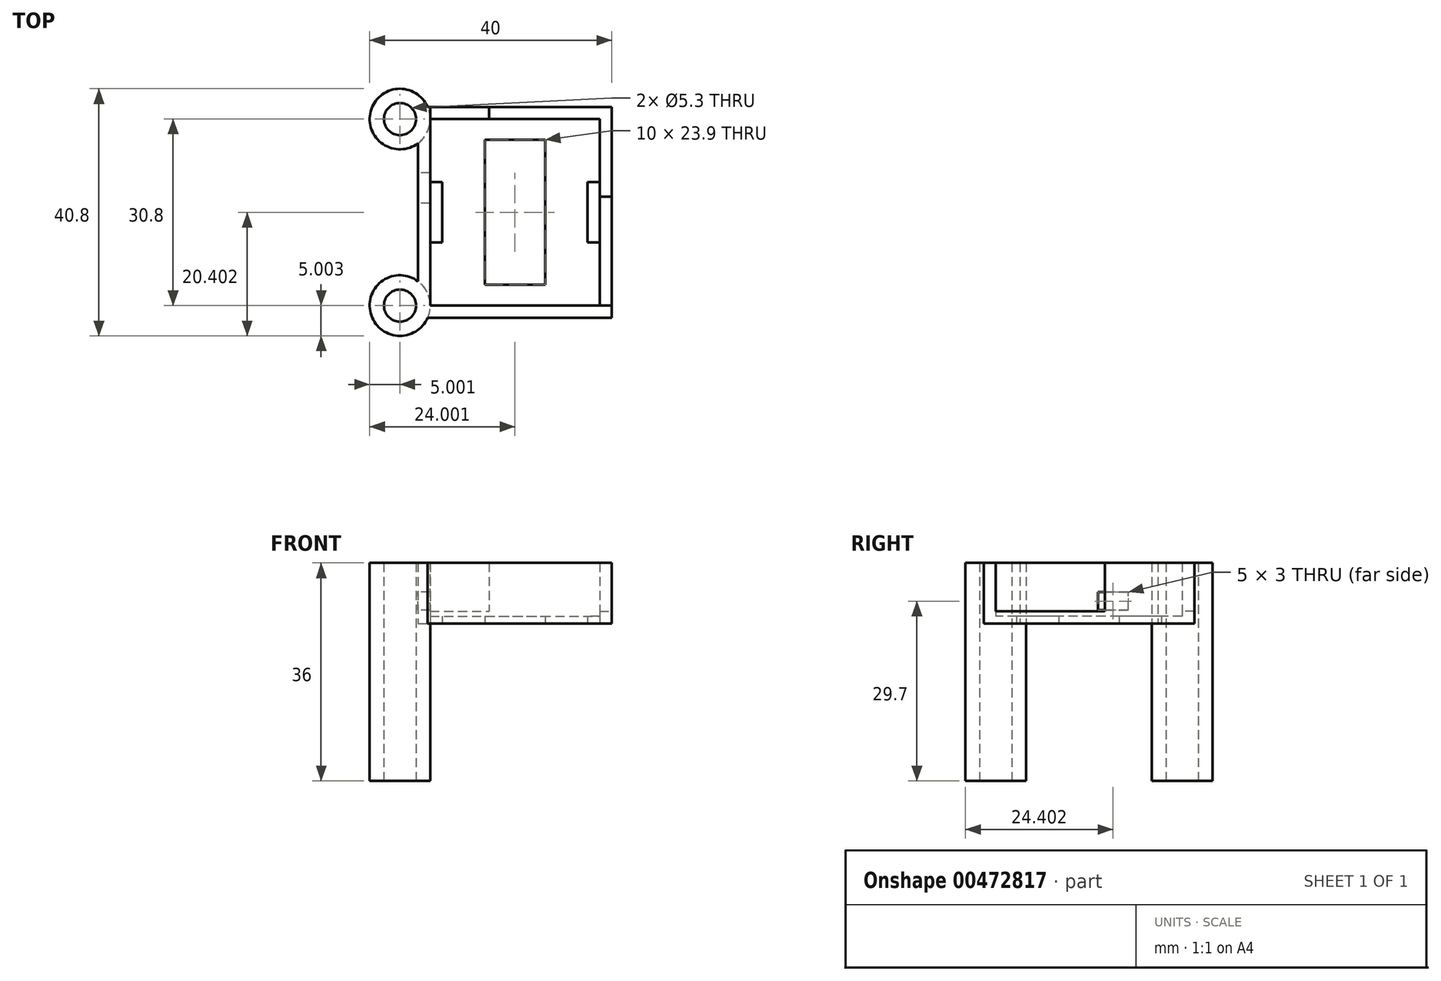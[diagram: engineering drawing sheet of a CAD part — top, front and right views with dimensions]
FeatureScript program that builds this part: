
annotation { "Feature Type Name" : "Feature", "Feature Type Description" : "" }
export const myFeature = defineFeature(function(context is Context, id is Id, definition is map)
    precondition{}
    {
        {
            var Q0;
            Q0=qCreatedBy(makeId("Top.planeOp"),FACE);
            var sketch = newSketch(context, id + "F0", { "sketchPlane" : qUnion([Q0])});
            skCircle(sketch, "E0", {"center": v(-36.74, -17.75) * mm, "radius": 5 * mm});
            skCircle(sketch, "E1", {"center": v(-36.74, 13.05) * mm, "radius": 5 * mm});
            skCircle(sketch, "E2", {"center": v(-36.74, -17.75) * mm, "radius": 2.65 * mm});
            skCircle(sketch, "E3", {"center": v(-36.74, 13.05) * mm, "radius": 2.65 * mm});
            skLineSegment(sketch, "E4", {"start": v(-36.74, 13.05) * mm, "end": v(-36.74, -17.75) * mm, "construction": true});
            skLineSegment(sketch, "E5.bottom", {"start": v(-31.74, 13.05) * mm, "end": v(-3.74, 13.05) * mm});
            skLineSegment(sketch, "E5.top", {"start": v(-31.74, -17.75) * mm, "end": v(-3.74, -17.75) * mm});
            skLineSegment(sketch, "E5.left", {"start": v(-31.74, 13.05) * mm, "end": v(-31.74, -17.75) * mm});
            skLineSegment(sketch, "E5.right", {"start": v(-3.74, 13.05) * mm, "end": v(-3.74, -17.75) * mm});
            skLineSegment(sketch, "E6", {"start": v(-36.74, -2.35) * mm, "end": v(-1.24, -2.35) * mm, "construction": true});
            skLineSegment(sketch, "E7", {"start": v(-17.74, 13.05) * mm, "end": v(-17.74, -17.75) * mm, "construction": true});
            skLineSegment(sketch, "E8.bottom", {"start": v(-33.74, 15.05) * mm, "end": v(-1.74, 15.05) * mm});
            skLineSegment(sketch, "E8.top", {"start": v(-33.74, -19.75) * mm, "end": v(-1.74, -19.75) * mm});
            skLineSegment(sketch, "E8.left", {"start": v(-33.74, 15.05) * mm, "end": v(-33.74, -19.75) * mm});
            skLineSegment(sketch, "E8.right", {"start": v(-1.74, 15.05) * mm, "end": v(-1.74, -19.75) * mm});
            skLineSegment(sketch, "E9.bottom", {"start": v(-22.74, 9.6) * mm, "end": v(-12.74, 9.6) * mm});
            skLineSegment(sketch, "E9.top", {"start": v(-22.74, -14.3) * mm, "end": v(-12.74, -14.3) * mm});
            skLineSegment(sketch, "E9.left", {"start": v(-22.74, 9.6) * mm, "end": v(-22.74, -14.3) * mm});
            skLineSegment(sketch, "E9.right", {"start": v(-12.74, 9.6) * mm, "end": v(-12.74, -14.3) * mm});
            skLineSegment(sketch, "E10.bottom", {"start": v(-3.74, 2.65) * mm, "end": v(-5.74, 2.65) * mm});
            skLineSegment(sketch, "E10.top", {"start": v(-3.74, -7.35) * mm, "end": v(-5.74, -7.35) * mm});
            skLineSegment(sketch, "E10.left", {"start": v(-3.74, 2.65) * mm, "end": v(-3.74, -7.35) * mm});
            skLineSegment(sketch, "E10.right", {"start": v(-5.74, 2.65) * mm, "end": v(-5.74, -7.35) * mm});
            skLineSegment(sketch, "E11.bottom", {"start": v(-31.74, 2.65) * mm, "end": v(-29.74, 2.65) * mm});
            skLineSegment(sketch, "E11.top", {"start": v(-31.74, -7.35) * mm, "end": v(-29.74, -7.35) * mm});
            skLineSegment(sketch, "E11.left", {"start": v(-31.74, 2.65) * mm, "end": v(-31.74, -7.35) * mm});
            skLineSegment(sketch, "E11.right", {"start": v(-29.74, 2.65) * mm, "end": v(-29.74, -7.35) * mm});
            skSolve(sketch);
        }
        {
            var Q0;
            Q0=makeQuery(id+"F0.imprint","IMPRINT",FACE,{"disambiguationData":[TD([[makeQuery(id+"F0.imprint","IMPRINT",EDGE,{"derivedFrom":sQuery(id+"F0.wireOp",EDGE,"E5.bottom")}),-1.0]])]});
            extrude(context, id + "F1", {"entities" : qUnion([Q0]), "depth" : 1.2 * mm});
        }
        {
            var Q0;
            {var subQ1=sQuery(id+"F0.wireOp",EDGE,"E5.bottom");Q0=makeQuery(id+"F0.imprint","IMPRINT",FACE,{"disambiguationData":[TD([[makeQuery(id+"F0.imprint","IMPRINT",EDGE,{"derivedFrom":subQ1}),1.0]])]});}
            var Q1;
            {var subQ0=sQuery(id+"F0.wireOp",EDGE,"E5.left");Q1=makeQuery(id+"F0.imprint","IMPRINT",FACE,{"disambiguationData":[TD([[makeQuery(id+"F0.imprint","IMPRINT",EDGE,{"derivedFrom":subQ0}),-1.0]])]});}
            var Q2;
            {var subQ2=sQuery(id+"F0.wireOp",EDGE,"E8.left");var subQ4=sQuery(id+"F0.wireOp",EDGE,"E8.bottom");var subQ6=makeQuery(id+"F0.imprint","INTERSECT",VERTEX,{"derivedFrom":[subQ4,subQ2]});Q2=makeQuery(id+"F0.imprint","IMPRINT",FACE,{"disambiguationData":[TD([[makeQuery(id+"F0.imprint","IMPRINT",EDGE,{"disambiguationData":[TD([[subQ6,-1.0]])],"derivedFrom":subQ4}),-1.0]])]});}
            var Q3;
            {var subQ0=sQuery(id+"F0.wireOp",EDGE,"E0");var subQ2=makeQuery(id+"F0.imprint","INTERSECT",VERTEX,{"derivedFrom":[subQ0,sQuery(id+"F0.wireOp",EDGE,"E5.left")]});Q3=makeQuery(id+"F0.imprint","IMPRINT",FACE,{"disambiguationData":[TD([[makeQuery(id+"F0.imprint","IMPRINT",EDGE,{"disambiguationData":[TD([[subQ2,-1.0]])],"derivedFrom":subQ0}),1.0]])]});}
            extrude(context, id + "F2", {"entities" : qUnion([Q0, Q1, Q2, Q3]), "operationType" : NewBodyOperationType.ADD, "depth" : 10 * mm});
        }
        {
            var Q0;
            Q0=makeQuery(id+"F0.imprint","IMPRINT",FACE,{"disambiguationData":[TD([[makeQuery(id+"F0.imprint","IMPRINT",EDGE,{"derivedFrom":sQuery(id+"F0.wireOp",EDGE,"E3")}),-1.0]])]});
            var Q1;
            Q1=makeQuery(id+"F0.imprint","IMPRINT",FACE,{"disambiguationData":[TD([[makeQuery(id+"F0.imprint","IMPRINT",EDGE,{"derivedFrom":sQuery(id+"F0.wireOp",EDGE,"E2")}),-1.0]])]});
            extrude(context, id + "F3", {"entities" : qUnion([Q0, Q1]), "operationType" : NewBodyOperationType.ADD, "depth" : 10 * mm});
        }
        {
            var Q0;
            Q0=makeQuery(id+"F0.imprint","IMPRINT",FACE,{"disambiguationData":[TD([[makeQuery(id+"F0.imprint","IMPRINT",EDGE,{"derivedFrom":sQuery(id+"F0.wireOp",EDGE,"E3")}),-1.0]])]});
            var Q1;
            {var subQ2=sQuery(id+"F0.wireOp",EDGE,"E8.left");var subQ4=sQuery(id+"F0.wireOp",EDGE,"E8.bottom");var subQ6=makeQuery(id+"F0.imprint","INTERSECT",VERTEX,{"derivedFrom":[subQ4,subQ2]});Q1=makeQuery(id+"F0.imprint","IMPRINT",FACE,{"disambiguationData":[TD([[makeQuery(id+"F0.imprint","IMPRINT",EDGE,{"disambiguationData":[TD([[subQ6,-1.0]])],"derivedFrom":subQ4}),-1.0]])]});}
            var Q2;
            Q2=makeQuery(id+"F0.imprint","IMPRINT",FACE,{"disambiguationData":[TD([[makeQuery(id+"F0.imprint","IMPRINT",EDGE,{"derivedFrom":sQuery(id+"F0.wireOp",EDGE,"E2")}),-1.0]])]});
            var Q3;
            {var subQ0=sQuery(id+"F0.wireOp",EDGE,"E0");var subQ2=makeQuery(id+"F0.imprint","INTERSECT",VERTEX,{"derivedFrom":[subQ0,sQuery(id+"F0.wireOp",EDGE,"E5.left")]});Q3=makeQuery(id+"F0.imprint","IMPRINT",FACE,{"disambiguationData":[TD([[makeQuery(id+"F0.imprint","IMPRINT",EDGE,{"disambiguationData":[TD([[subQ2,-1.0]])],"derivedFrom":subQ0}),1.0]])]});}
            extrude(context, id + "F4", {"entities" : qUnion([Q0, Q1, Q2, Q3]), "operationType" : NewBodyOperationType.ADD, "oppositeDirection" : true, "depth" : 26 * mm});
        }
        {
            var Q0;
            Q0=makeQuery(id+"F2.opExtrude","SWEPT_FACE",FACE,{"disambiguationData":[OSD([sQuery(id+"F0.wireOp",EDGE,"E8.right")])]});
            var sketch = newSketch(context, id + "F5", { "sketchPlane" : qUnion([Q0])});
            skLineSegment(sketch, "E12.bottom", {"start": v(-17.75, 10) * mm, "end": v(0.25, 10) * mm});
            skLineSegment(sketch, "E12.top", {"start": v(-17.75, 2) * mm, "end": v(0.25, 2) * mm});
            skLineSegment(sketch, "E12.left", {"start": v(-17.75, 10) * mm, "end": v(-17.75, 2) * mm});
            skLineSegment(sketch, "E12.right", {"start": v(0.25, 10) * mm, "end": v(0.25, 2) * mm});
            skSolve(sketch);
        }
        {
            var Q0;
            Q0=makeQuery(id+"F5.imprint","IMPRINT",FACE,{"disambiguationData":[TD([[makeQuery(id+"F5.imprint","IMPRINT",EDGE,{"derivedFrom":sQuery(id+"F5.wireOp",EDGE,"E12.bottom")}),1.0]])]});
            extrude(context, id + "F6", {"entities" : qUnion([Q0]), "operationType" : NewBodyOperationType.REMOVE, "oppositeDirection" : true, "depth" : 3 * mm});
        }
        {
            var Q0;
            Q0=makeQuery(id+"F2.opExtrude","SWEPT_FACE",FACE,{"disambiguationData":[OSD([sQuery(id+"F0.wireOp",EDGE,"E5.bottom")])]});
            var sketch = newSketch(context, id + "F7", { "sketchPlane" : qUnion([Q0])});
            skLineSegment(sketch, "E13.bottom", {"start": v(-31.74, 10) * mm, "end": v(-22.04, 10) * mm});
            skLineSegment(sketch, "E13.top", {"start": v(-31.74, 2) * mm, "end": v(-22.04, 2) * mm});
            skLineSegment(sketch, "E13.left", {"start": v(-31.74, 10) * mm, "end": v(-31.74, 2) * mm});
            skLineSegment(sketch, "E13.right", {"start": v(-22.04, 10) * mm, "end": v(-22.04, 2) * mm});
            skSolve(sketch);
        }
        {
            var Q0;
            Q0=makeQuery(id+"F7.imprint","IMPRINT",FACE,{"disambiguationData":[TD([[makeQuery(id+"F7.imprint","IMPRINT",EDGE,{"derivedFrom":sQuery(id+"F7.wireOp",EDGE,"E13.bottom")}),-1.0]])]});
            extrude(context, id + "F8", {"entities" : qUnion([Q0]), "operationType" : NewBodyOperationType.REMOVE, "oppositeDirection" : true, "depth" : 25 * mm});
        }
        {
            var Q0;
            Q0=makeQuery(id+"F2.opExtrude","SWEPT_FACE",FACE,{"disambiguationData":[OSD([sQuery(id+"F0.wireOp",EDGE,"E8.left")])]});
            var sketch = newSketch(context, id + "F9", { "sketchPlane" : qUnion([Q0])});
            skLineSegment(sketch, "E14", {"start": v(2.35, 0) * mm, "end": v(2.35, 10) * mm, "construction": true});
            skLineSegment(sketch, "E15.bottom", {"start": v(-4.15, 2.2) * mm, "end": v(0.85, 2.2) * mm});
            skLineSegment(sketch, "E15.top", {"start": v(-4.15, 5.2) * mm, "end": v(0.85, 5.2) * mm});
            skLineSegment(sketch, "E15.left", {"start": v(-4.15, 2.2) * mm, "end": v(-4.15, 5.2) * mm});
            skLineSegment(sketch, "E15.right", {"start": v(0.85, 2.2) * mm, "end": v(0.85, 5.2) * mm});
            skSolve(sketch);
        }
        {
            var Q0;
            Q0=makeQuery(id+"F9.imprint","IMPRINT",FACE,{"disambiguationData":[TD([[makeQuery(id+"F9.imprint","IMPRINT",EDGE,{"derivedFrom":sQuery(id+"F9.wireOp",EDGE,"E15.bottom")}),1.0]])]});
            extrude(context, id + "F10", {"entities" : qUnion([Q0]), "operationType" : NewBodyOperationType.REMOVE, "oppositeDirection" : true, "depth" : 4 * mm});
        }
    });
